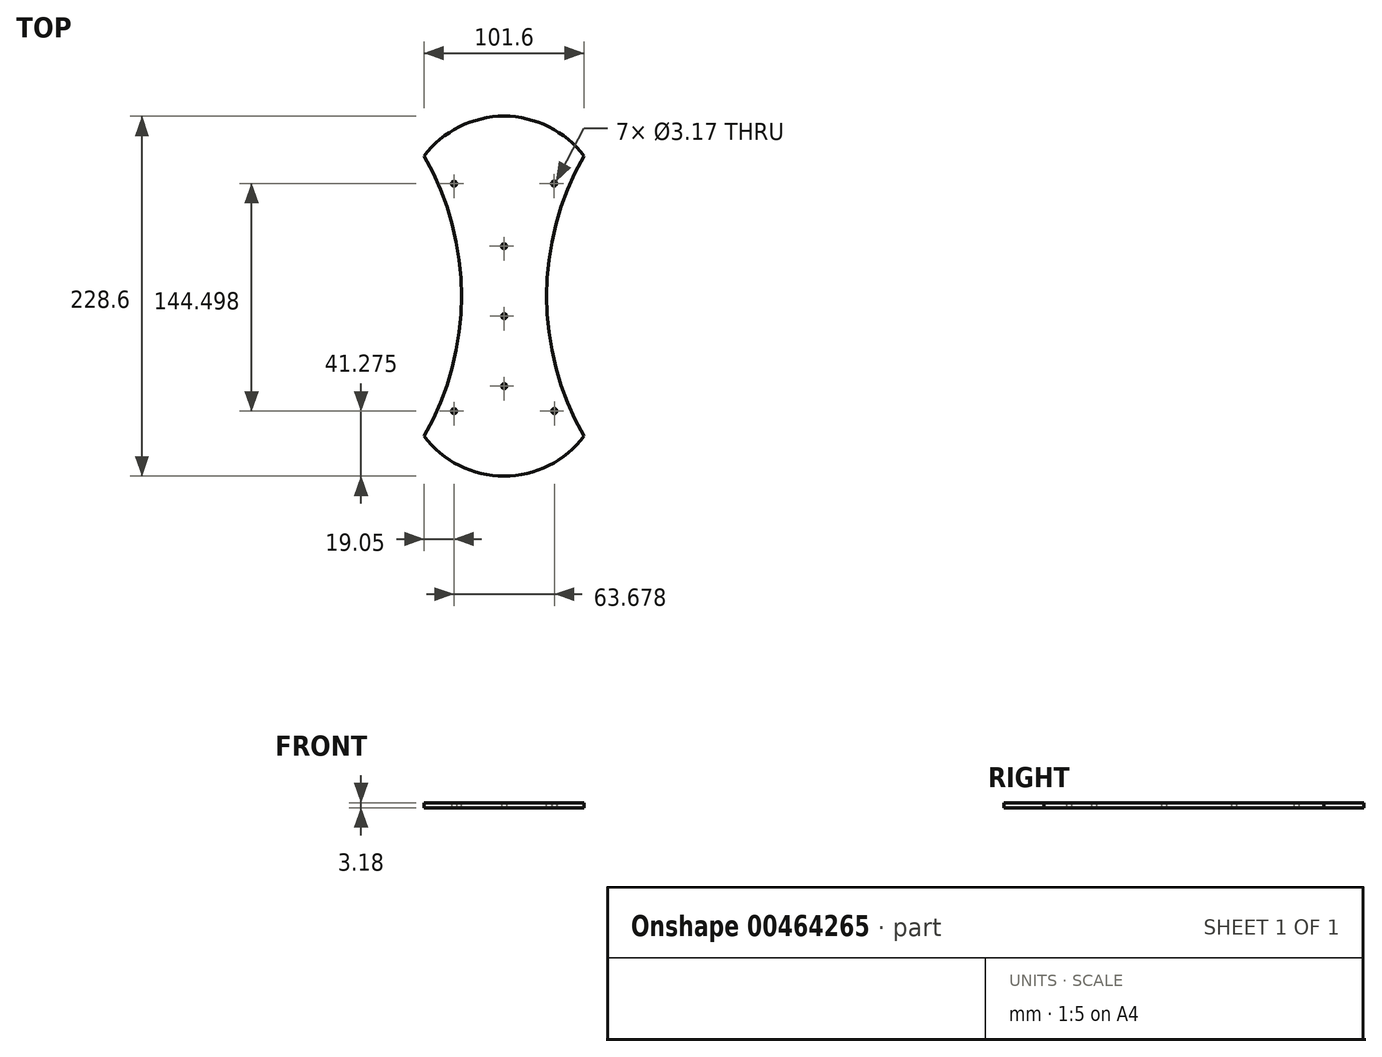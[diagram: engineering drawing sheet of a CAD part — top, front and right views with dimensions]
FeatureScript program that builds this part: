
annotation { "Feature Type Name" : "Feature", "Feature Type Description" : "" }
export const myFeature = defineFeature(function(context is Context, id is Id, definition is map)
    precondition{}
    {
        {
            var Q0;
            Q0=qCreatedBy(makeId("Top.planeOp"),FACE);
            var sketch = newSketch(context, id + "F0", { "sketchPlane" : qUnion([Q0])});
            skCircle(sketch, "E0", {"center": v(50.8, 120.65) * mm, "radius": 31.75 * mm, "construction": true});
            skCircle(sketch, "E1", {"center": v(50.9, 76.2) * mm, "radius": 31.75 * mm, "construction": true});
            skCircle(sketch, "E2", {"center": v(50.9, 76.2) * mm, "radius": 12.7 * mm, "construction": true});
            skCircle(sketch, "E3", {"center": v(50.9, 31.75) * mm, "radius": 12.7 * mm, "construction": true});
            skCircle(sketch, "E4", {"center": v(50.9, 31.75) * mm, "radius": 1.59 * mm});
            skCircle(sketch, "E5", {"center": v(50.8, 120.65) * mm, "radius": 1.59 * mm});
            skCircle(sketch, "E6", {"center": v(50.9, 76.2) * mm, "radius": 1.59 * mm});
            skLineSegment(sketch, "E7.bottom", {"start": v(0, 177.8) * mm, "end": v(101.6, 177.8) * mm});
            skLineSegment(sketch, "E7.top", {"start": v(0, 0) * mm, "end": v(101.6, 0) * mm});
            skLineSegment(sketch, "E7.left", {"start": v(0, 177.8) * mm, "end": v(0, 0) * mm});
            skLineSegment(sketch, "E7.right", {"start": v(101.6, 177.8) * mm, "end": v(101.6, 0) * mm});
            skLineSegment(sketch, "E8", {"start": v(50.8, 177.8) * mm, "end": v(50.9, 0) * mm, "construction": true});
            skCircle(sketch, "E9", {"center": v(19.05, 15.88) * mm, "radius": 1.59 * mm});
            skCircle(sketch, "E10", {"center": v(19.05, 160.34) * mm, "radius": 1.59 * mm});
            skCircle(sketch, "E11.MirrorC", {"center": v(82.57, 160.37) * mm, "radius": 1.59 * mm});
            skCircle(sketch, "E12.MirrorC", {"center": v(82.73, 15.91) * mm, "radius": 1.59 * mm});
            skCircle(sketch, "E13", {"center": v(19.05, 160.34) * mm, "radius": 19.05 * mm, "construction": true});
            skCircle(sketch, "E14", {"center": v(82.57, 160.37) * mm, "radius": 19.05 * mm, "construction": true});
            skSolve(sketch);
        }
        {
            var Q0;
            Q0=makeQuery(id+"F0.imprint","IMPRINT",FACE,{"disambiguationData":[TD([[makeQuery(id+"F0.imprint","IMPRINT",EDGE,{"derivedFrom":sQuery(id+"F0.wireOp",EDGE,"E4")}),-1.0]])]});
            extrude(context, id + "F1", {"entities" : qUnion([Q0]), "depth" : 3.17 * mm, "offsetDistance" : 25.4 * mm});
        }
        {
            var Q0;
            Q0=makeQuery(id+"F1.opExtrude","CAP_FACE",FACE,{"disambiguationData":[OSD([sQuery(id+"F0.wireOp",EDGE,"E4"),sQuery(id+"F0.wireOp",EDGE,"E5"),sQuery(id+"F0.wireOp",EDGE,"E6"),sQuery(id+"F0.wireOp",EDGE,"E7.bottom"),sQuery(id+"F0.wireOp",EDGE,"E7.top"),sQuery(id+"F0.wireOp",EDGE,"E7.left"),sQuery(id+"F0.wireOp",EDGE,"E7.right"),sQuery(id+"F0.wireOp",EDGE,"E9"),sQuery(id+"F0.wireOp",EDGE,"E10"),sQuery(id+"F0.wireOp",EDGE,"E11.MirrorC"),sQuery(id+"F0.wireOp",EDGE,"E12.MirrorC")])],"isStart":false});
            var sketch = newSketch(context, id + "F2", { "sketchPlane" : qUnion([Q0])});
            skArc(sketch, "E15", {"start": v(101.6, 177.8) * mm, "mid": v(77.78, 88.9) * mm, "end": v(101.6, 0) * mm});
            skArc(sketch, "E16", {"start": v(0, 0) * mm, "mid": v(23.82, 88.9) * mm, "end": v(0, 177.8) * mm});
            skSolve(sketch);
        }
        {
            var Q0;
            {var subQ0=sQuery(id+"F2.wireOp",EDGE,"E15");Q0=makeQuery(id+"F2.imprint","IMPRINT",FACE,{"disambiguationData":[TD([[makeQuery(id+"F2.imprint","IMPRINT",EDGE,{"derivedFrom":subQ0}),1.0]])]});}
            var Q1;
            {var subQ0=sQuery(id+"F2.wireOp",EDGE,"E16");Q1=makeQuery(id+"F2.imprint","IMPRINT",FACE,{"disambiguationData":[TD([[makeQuery(id+"F2.imprint","IMPRINT",EDGE,{"derivedFrom":subQ0}),1.0]])]});}
            extrude(context, id + "F3", {"entities" : qUnion([Q0, Q1]), "operationType" : NewBodyOperationType.REMOVE, "oppositeDirection" : true, "depth" : 25.4 * mm, "offsetDistance" : 25.4 * mm});
        }
        {
            var Q0;
            Q0=makeQuery(id+"F1.opExtrude","CAP_FACE",FACE,{"disambiguationData":[OSD([sQuery(id+"F0.wireOp",EDGE,"E4"),sQuery(id+"F0.wireOp",EDGE,"E5"),sQuery(id+"F0.wireOp",EDGE,"E6"),sQuery(id+"F0.wireOp",EDGE,"E7.bottom"),sQuery(id+"F0.wireOp",EDGE,"E7.top"),sQuery(id+"F0.wireOp",EDGE,"E7.left"),sQuery(id+"F0.wireOp",EDGE,"E7.right"),sQuery(id+"F0.wireOp",EDGE,"E9"),sQuery(id+"F0.wireOp",EDGE,"E10"),sQuery(id+"F0.wireOp",EDGE,"E11.MirrorC"),sQuery(id+"F0.wireOp",EDGE,"E12.MirrorC")])],"isStart":false});
            var sketch = newSketch(context, id + "F4", { "sketchPlane" : qUnion([Q0])});
            skArc(sketch, "E17", {"start": v(101.6, 177.8) * mm, "mid": v(50.8, 203.2) * mm, "end": v(0, 177.8) * mm});
            skArc(sketch, "E18", {"start": v(0, 0) * mm, "mid": v(50.8, -25.4) * mm, "end": v(101.6, 0) * mm});
            skSolve(sketch);
        }
        {
            var Q0;
            Q0=makeQuery(id+"F4.imprint","IMPRINT",FACE,{"disambiguationData":[TD([[makeQuery(id+"F4.imprint","IMPRINT",EDGE,{"derivedFrom":sQuery(id+"F4.wireOp",EDGE,"E17")}),1.0]])]});
            var Q1;
            Q1=makeQuery(id+"F4.imprint","IMPRINT",FACE,{"disambiguationData":[TD([[makeQuery(id+"F4.imprint","IMPRINT",EDGE,{"derivedFrom":sQuery(id+"F4.wireOp",EDGE,"E18")}),1.0]])]});
            var Q2;
            Q2=makeQuery(id+"F1.opExtrude","CAP_FACE",FACE,{"disambiguationData":[OSD([sQuery(id+"F0.wireOp",EDGE,"E4"),sQuery(id+"F0.wireOp",EDGE,"E5"),sQuery(id+"F0.wireOp",EDGE,"E6"),sQuery(id+"F0.wireOp",EDGE,"E7.bottom"),sQuery(id+"F0.wireOp",EDGE,"E7.top"),sQuery(id+"F0.wireOp",EDGE,"E7.left"),sQuery(id+"F0.wireOp",EDGE,"E7.right"),sQuery(id+"F0.wireOp",EDGE,"E9"),sQuery(id+"F0.wireOp",EDGE,"E10"),sQuery(id+"F0.wireOp",EDGE,"E11.MirrorC"),sQuery(id+"F0.wireOp",EDGE,"E12.MirrorC")])],"isStart":true});
            extrude(context, id + "F5", {"entities" : qUnion([Q0, Q1]), "operationType" : NewBodyOperationType.ADD, "endBound" : BoundingType.UP_TO_SURFACE, "oppositeDirection" : true, "depth" : 25.4 * mm, "endBoundEntityFace" : qUnion([Q2]), "offsetDistance" : 25.4 * mm});
        }
    });
